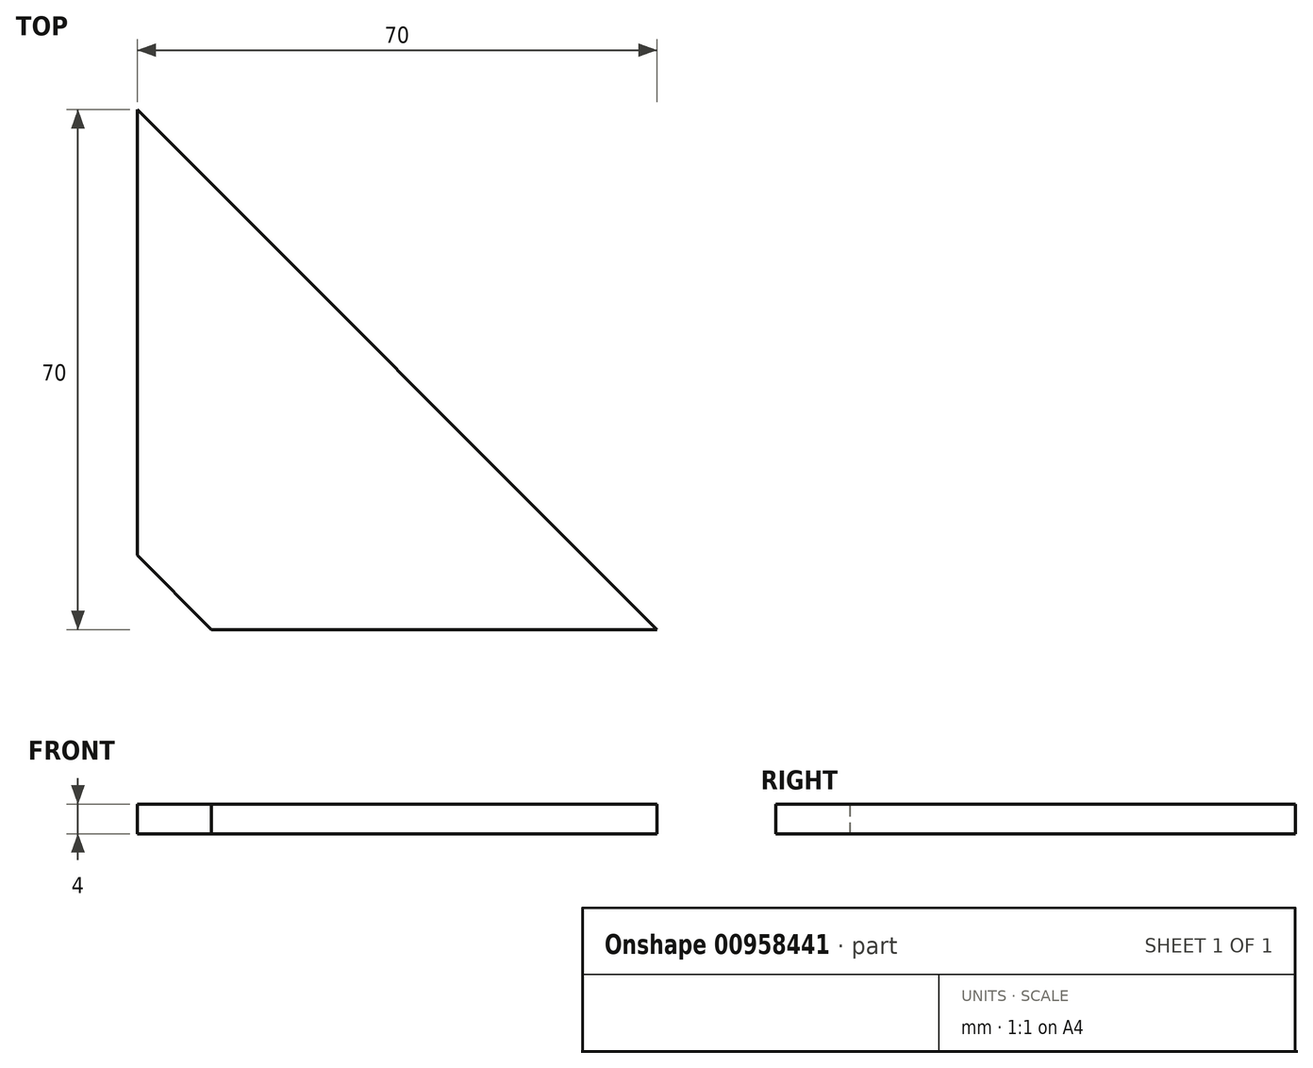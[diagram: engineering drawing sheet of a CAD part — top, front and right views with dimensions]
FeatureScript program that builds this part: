
annotation { "Feature Type Name" : "Feature", "Feature Type Description" : "" }
export const myFeature = defineFeature(function(context is Context, id is Id, definition is map)
    precondition{}
    {
        {
            var Q0;
            Q0=qCreatedBy(makeId("Top.planeOp"),FACE);
            var sketch = newSketch(context, id + "F0", { "sketchPlane" : qUnion([Q0])});
            skLineSegment(sketch, "E0", {"start": v(0, 0) * mm, "end": v(0, 70) * mm});
            skLineSegment(sketch, "E1", {"start": v(0, 0) * mm, "end": v(70, 0) * mm});
            skLineSegment(sketch, "E2", {"start": v(70, 0) * mm, "end": v(0, 70) * mm});
            skSolve(sketch);
        }
        {
            var Q0;
            Q0=makeQuery(id+"F0.imprint","IMPRINT",FACE,{"disambiguationData":[TD([[makeQuery(id+"F0.imprint","IMPRINT",EDGE,{"derivedFrom":sQuery(id+"F0.wireOp",EDGE,"E0")}),-1.0]])]});
            extrude(context, id + "F1", {"entities" : qUnion([Q0]), "depth" : 4 * mm, "offsetDistance" : 25 * mm});
        }
        {
            var Q0;
            Q0=makeQuery(id+"F1.opExtrude","SWEPT_EDGE",EDGE,{"disambiguationData":[OSD([sQuery(id+"F0.wireOp",EDGE,"E0"),sQuery(id+"F0.wireOp",EDGE,"E1")])]});
            chamfer(context, id + "F2", {"entities" : qUnion([Q0]), "width" : 10 * mm, "tangentPropagation" : true});
        }
    });
